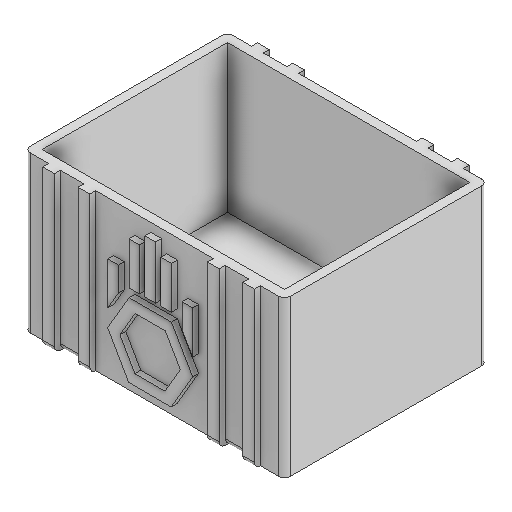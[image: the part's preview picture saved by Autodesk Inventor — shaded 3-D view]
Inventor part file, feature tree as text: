
AUTODESK INVENTOR PART (.ipt)
format: ipt  version: 2025.1 (Build 291241020, 241B)  size: 270,336 bytes
history: native  units: in
note: dims shown in document units (in); Inventor stores cm internally (conversion verified against a paired STEP export)
features: extrude x3, sketch x3, fillet x2, shell x1, plane x1, mirror x1
ambient origin geometry x8: Origin, YZ Plane, XZ Plane, XY Plane, X Axis, Y Axis, Z Axis, Center Point
bodies: Solid1 (feature_tree)
feature tree (11):
  extrude  "Extrusion1"  Depth=2.65in
  shell  "Shell1"  Thickness=3.45in
  extrude  "Extrusion2"  Depth=0.2in
  plane  "Work Plane1"
  mirror  "Mirror1"
  fillet  "Fillet1"  Radius=0.2in
  extrude  "Extrusion3"  Depth=0.2in
  fillet  "Fillet2"  Radius=0.4in
  sketch  "Sketch1"  dims[d0=4.42in d1=2.65in d2=3.45in d3=0.0in]
  sketch  "Sketch2"  dims[d4=0.15in d5=0.2in d6=0.2in]
  sketch  "Sketch3"  dims[d7=0.2in d8=0.2in d9=0.4in d10=0.4in d11=2.0in d12=1.0in d13=0.1in d14=0.0in d15=0.1in d16=0.721in d17=0.1803in d18=0.1442in d19=0.1442in d20=0.1803in d21=0.1803in d22=0.1803in d23=0.1803in d24=0.1442in d25=0.7211in d26=0.7211in d27=0.9013in d28=0.1803in d29=0.1803in d30=0.1803in d31=0.0901in d32=-0.181in d33=0.9779in d34=0.1in d35=0.0in d36=0.1in]
